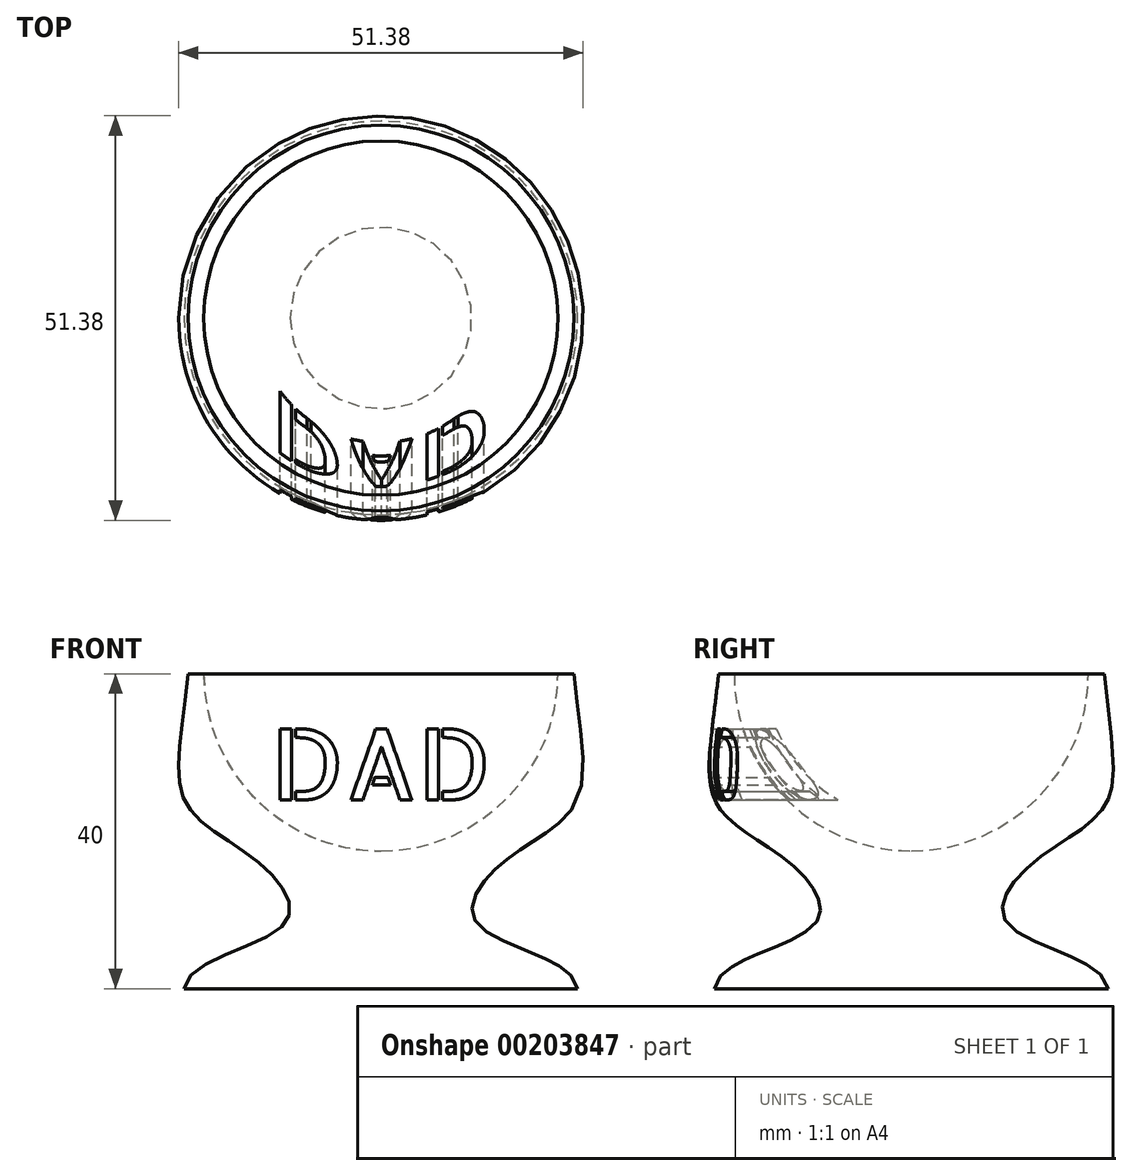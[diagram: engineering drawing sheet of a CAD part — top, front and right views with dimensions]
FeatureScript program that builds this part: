
annotation { "Feature Type Name" : "Feature", "Feature Type Description" : "" }
export const myFeature = defineFeature(function(context is Context, id is Id, definition is map)
    precondition{}
    {
        {
            var Q0;
            Q0=qCreatedBy(makeId("Front.planeOp"),FACE);
            var sketch = newSketch(context, id + "F0", { "sketchPlane" : qUnion([Q0])});
            skLineSegment(sketch, "E0", {"start": v(-25, 0) * mm, "end": v(0, 0) * mm});
            skLineSegment(sketch, "E1", {"start": v(0, 0) * mm, "end": v(0, 40) * mm});
            skCircle(sketch, "E2", {"center": v(0, 40) * mm, "radius": 22.5 * mm});
            skLineSegment(sketch, "E3", {"start": v(-22.5, 40) * mm, "end": v(-24.5, 40) * mm});
            skFitSpline(sketch, "E4", {"points": [v(-24.5, 40) * mm, v(-24.66, 23.38) * mm, v(-15.34, 15.89) * mm, v(-12.24, 8.22) * mm, v(-25, 0) * mm], "startDerivative": vector(-7.63, -82.06) * mm, "endDerivative": vector(-4.3, -42.94) * mm});
            skSolve(sketch);
        }
        {
            var Q0;
            {var subQ4=sQuery(id+"F0.wireOp",EDGE,"E0");Q0=makeQuery(id+"F0.imprint","IMPRINT",FACE,{"disambiguationData":[TD([[makeQuery(id+"F0.imprint","IMPRINT",EDGE,{"derivedFrom":subQ4}),1.0]])]});}
            var Q1;
            Q1=sQuery(id+"F0.wireOp",EDGE,"E1");
            revolve(context, id + "F1", {"entities" : qUnion([Q0]), "axis" : qUnion([Q1]), "revolveType" : RevolveType.FULL});
        }
        {
            var Q0;
            Q0=qCreatedBy(makeId("Front.planeOp"),FACE);
            var sketch = newSketch(context, id + "F2", { "sketchPlane" : qUnion([Q0])});
            skText(sketch, "E5", { "text": "DAD", "fontName": "AllertaStencil-Regular.ttf"});
            skLineSegment(sketch, "E6", {"start": v(0, 24) * mm, "end": v(0, 0) * mm, "construction": true});
            const initialGuessF2  = {"E5": [-0.01397, 0.024, 1, 0, 0.009]};
            skSetInitialGuess(sketch, initialGuessF2);
            skSolve(sketch);
        }
        {
            var Q0;
            Q0 = qSketchRegion(id + "F2", true);
            extrude(context, id + "F3", {"entities" : qUnion([Q0]), "operationType" : NewBodyOperationType.REMOVE, "depth" : 29.8 * mm});
        }
    });
